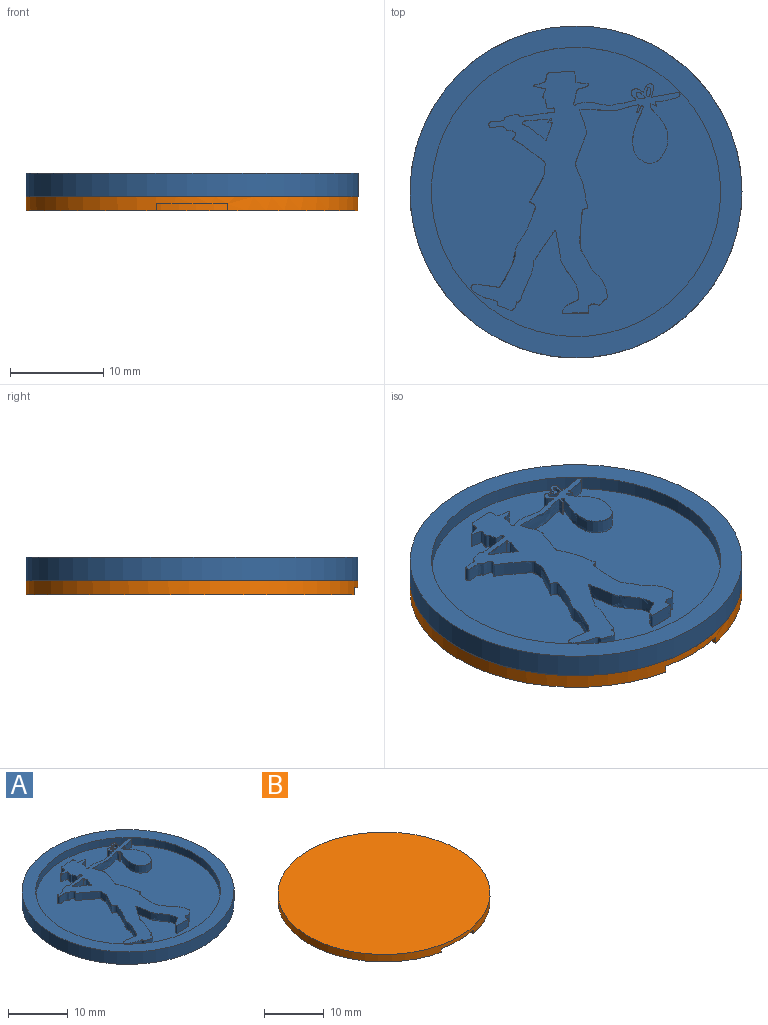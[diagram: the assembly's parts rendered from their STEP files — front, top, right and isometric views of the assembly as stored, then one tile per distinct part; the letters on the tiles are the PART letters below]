
ASSEMBLY  parts=2 mates=1
PART A: 13 faces, bbox 35.6x35.6x2.5 mm
  f0: plane 30.99x30.99mm, normal (0,0,1), area 683.6mm2, adj f4,f7
  f1: cylinder r=17.78mm len=35.56mm, axis (0,0,-1), area 283.8mm2, adj f2,f3
  f2: plane 35.56x35.56mm, normal (0,0,1), area 239mm2, adj f1,f4
  f3: plane 35.56x35.56mm, normal (0,0,-1), area 993.1mm2, adj f1
  f4: cylinder r=15.49mm len=30.99mm, axis (0,0,1), area 148.4mm2, adj f0,f2
  f5: plane 26x22.42mm, normal (0,0,1), area 87.5mm2, adj f6,f7,f8,f9
  f6: extruded ~1.52x1.02mm, area 3.8mm2, adj f5,f11
  f7: extruded ~25.78x19.35mm, area 227.5mm2, adj f0,f5
  f8: extruded ~1.52x1.02mm, area 4.2mm2, adj f5,f12
  f9: extruded ~3.18x2.29mm, area 14.9mm2, adj f5,f10
  f10: plane 3.23x2.33mm, normal (0,0,1), area 4mm2, adj f9
  f11: plane 1.03x0.46mm, normal (0,0,1), area 0.3mm2, adj f6
  f12: plane 1.03x0.75mm, normal (0,0,1), area 0.5mm2, adj f8
PART B: 170 faces, bbox 35.6x35.6x1.5 mm
  f0: plane 30.99x30.99mm, normal (0,0,-1), area 549.6mm2, adj f4,f5,f6,f7,f8,f9,f10,f11
  f1: plane 35.56x35.15mm, normal (0,0,-1), area 175mm2, adj f2,f165,f167,f169
  f2: cylinder r=17.78mm len=35.56mm, axis (0,0,-1), area 164.4mm2, adj f1,f3,f165,f167,f168
  f3: plane 35.56x35.56mm, normal (0,0,1), area 993.1mm2, adj f2
  f4: plane 1.49x0.76mm, normal (0,-1,0), area 1.1mm2, adj f0,f5,f15,f16
  f5: plane 7.05x0.76mm, normal (-1,0,0), area 5.4mm2, adj f0,f4,f6,f16
  f6: plane 1.49x0.76mm, normal (0,1,0), area 1.1mm2, adj f0,f5,f7,f16
  f7: plane 2.76x0.76mm, normal (1,0,0), area 2.1mm2, adj f0,f6,f8,f16
  f8: plane 2.79x0.76mm, normal (0,1,0), area 2.1mm2, adj f0,f7,f9,f16
  f9: plane 2.76x0.76mm, normal (-1,0,0), area 2.1mm2, adj f0,f8,f10,f16
  f10: plane 1.5x0.76mm, normal (0,1,0), area 1.1mm2, adj f0,f9,f11,f16
  f11: plane 7.05x0.76mm, normal (1,0,0), area 5.4mm2, adj f0,f10,f12,f16
  f12: plane 1.5x0.76mm, normal (0,-1,0), area 1.1mm2, adj f0,f11,f13,f16
  f13: plane 3.04x0.76mm, normal (-1,0,0), area 2.3mm2, adj f0,f12,f14,f16
  f14: plane 2.79x0.76mm, normal (0,-1,0), area 2.1mm2, adj f0,f13,f15,f16
  f15: plane 3.04x0.76mm, normal (1,0,0), area 2.3mm2, adj f0,f4,f14,f16
  f16: plane 7.05x5.78mm, normal (0,0,-1), area 24.5mm2, adj f4,f5,f6,f7,f8,f9,f10,f11
  f17: plane 7.05x0.76mm, normal (-1,0,0), area 5.4mm2, adj f0,f18,f41,f42
  f18: plane 2.19x0.76mm, normal (0,1,0), area 1.7mm2, adj f0,f17,f19,f42
  f19: extruded ~2.18x0.76mm, area 1.7mm2, adj f0,f18,f20,f42
  f20: extruded ~1.36x0.76mm, area 1.2mm2, adj f0,f19,f21,f42
  f21: extruded ~1.04x0.76mm, area 0.8mm2, adj f0,f20,f22,f42
  f22: extruded ~0.79x0.76mm, area 0.7mm2, adj f0,f21,f23,f42
  f23: plane 0.76x0.05mm, normal (1,0,0), area 0mm2, adj f0,f22,f24,f42
  f24: extruded ~0.97x0.76mm, area 0.9mm2, adj f0,f23,f25,f42
  f25: extruded ~1.09x0.76mm, area 0.9mm2, adj f0,f24,f26,f42
  f26: extruded ~1.51x0.76mm, area 1.3mm2, adj f0,f25,f27,f42
  f27: extruded ~1.89x0.76mm, area 1.5mm2, adj f0,f26,f41,f42
  f28: plane 0.93x0.76mm, normal (0,-1,0), area 0.7mm2, adj f29,f39,f42,f44
  f29: plane 1.84x0.76mm, normal (1,0,0), area 1.4mm2, adj f28,f30,f42,f44
  f30: plane 0.97x0.76mm, normal (0,1,0), area 0.7mm2, adj f29,f31,f42,f44
  f31: extruded ~0.91x0.76mm, area 0.7mm2, adj f30,f32,f42,f44
  f32: extruded ~0.76x0.72mm, area 0.6mm2, adj f31,f39,f42,f44
  f33: plane 1.57x0.76mm, normal (1,0,0), area 1.2mm2, adj f34,f40,f42,f43
  f34: plane 0.87x0.76mm, normal (0,1,0), area 0.7mm2, adj f33,f35,f42,f43
  f35: extruded ~0.88x0.76mm, area 0.7mm2, adj f34,f36,f42,f43
  f36: extruded ~0.76x0.62mm, area 0.5mm2, adj f35,f37,f42,f43
  f37: extruded ~0.76x0.58mm, area 0.5mm2, adj f36,f38,f42,f43
  f38: extruded ~0.94x0.76mm, area 0.7mm2, adj f37,f40,f42,f43
  f39: extruded ~1.25x0.88mm, area 1.3mm2, adj f28,f32,f42,f44
  f40: plane 0.79x0.76mm, normal (0,-1,0), area 0.6mm2, adj f33,f38,f42,f43
  f41: plane 2.64x0.76mm, normal (0,-1,0), area 2mm2, adj f0,f17,f27,f42
  f42: plane 7.05x5.23mm, normal (0,0,-1), area 27.1mm2, adj f17,f18,f19,f20,f21,f22,f23,f24
  f43: plane 2.02x1.57mm, normal (0,0,-1), area 2.9mm2, adj f33,f34,f35,f36,f37,f38,f40
  f44: plane 2.18x1.84mm, normal (0,0,-1), area 3.6mm2, adj f28,f29,f30,f31,f32,f39
  f45: extruded ~2.44x2.09mm, area 2.8mm2, adj f0,f46,f52,f53
  f46: extruded ~2.44x2.09mm, area 2.8mm2, adj f0,f45,f47,f53
  f47: extruded ~2.41x2.09mm, area 2.7mm2, adj f0,f46,f52,f53
  f48: extruded ~1.63x1.14mm, area 1.7mm2, adj f49,f51,f53,f54
  f49: extruded ~1.63x1.14mm, area 1.7mm2, adj f48,f50,f53,f54
  f50: extruded ~1.6x1.14mm, area 1.7mm2, adj f49,f51,f53,f54
  f51: extruded ~1.6x1.14mm, area 1.7mm2, adj f48,f50,f53,f54
  f52: extruded ~2.41x2.09mm, area 2.7mm2, adj f0,f45,f47,f53
  f53: plane 4.85x4.18mm, normal (0,0,-1), area 10.4mm2, adj f45,f46,f47,f48,f49,f50,f51,f52
  f54: plane 3.24x2.27mm, normal (0,0,-1), area 6mm2, adj f48,f49,f50,f51
  f55: extruded ~1.45x0.82mm, area 1.3mm2, adj f0,f56,f62,f63
  f56: extruded ~1.6x1.45mm, area 1.9mm2, adj f0,f55,f57,f63
  f57: plane 3.16x0.76mm, normal (-1,0,0), area 2.4mm2, adj f0,f56,f58,f63
  f58: plane 0.93x0.76mm, normal (0,1,0), area 0.7mm2, adj f0,f57,f59,f63
  f59: plane 3.09x0.76mm, normal (1,0,0), area 2.4mm2, adj f0,f58,f60,f63
  f60: extruded ~0.86x0.76mm, area 0.9mm2, adj f0,f59,f61,f63
  f61: extruded ~0.76x0.69mm, area 0.7mm2, adj f0,f60,f62,f63
  f62: plane 0.76x0.64mm, normal (0.59,0.81,0), area 0.6mm2, adj f0,f55,f61,f63
  f63: plane 4.76x2.9mm, normal (0,0,-1), area 5.6mm2, adj f55,f56,f57,f58,f59,f60,f61,f62
  f64: extruded ~2.19x1.82mm, area 2.5mm2, adj f0,f65,f73,f74
  f65: extruded ~2.19x1.81mm, area 2.5mm2, adj f0,f64,f66,f74
  f66: plane 2.57x0.76mm, normal (-1,0,0), area 2mm2, adj f0,f65,f67,f74
  f67: plane 0.9x0.76mm, normal (0,1,0), area 0.7mm2, adj f0,f66,f68,f74
  f68: plane 2.65x0.76mm, normal (1,0,0), area 2mm2, adj f0,f67,f69,f74
  f69: extruded ~1.3x0.91mm, area 1.4mm2, adj f0,f68,f70,f74
  f70: extruded ~1.3x0.88mm, area 1.4mm2, adj f0,f69,f71,f74
  f71: plane 2.65x0.76mm, normal (-1,0,0), area 2mm2, adj f0,f70,f72,f74
  f72: plane 0.93x0.76mm, normal (0,1,0), area 0.7mm2, adj f0,f71,f73,f74
  f73: plane 2.57x0.76mm, normal (1,0,0), area 2mm2, adj f0,f64,f72,f74
  f74: plane 4.76x3.62mm, normal (0,0,-1), area 9.2mm2, adj f64,f65,f66,f67,f68,f69,f70,f71
  f75: plane 4.67x0.76mm, normal (1,0,0), area 3.6mm2, adj f0,f76,f90,f91
  f76: plane 0.88x0.76mm, normal (0,-1,0), area 0.7mm2, adj f0,f75,f77,f91
  f77: plane 1.88x0.76mm, normal (-1,0,0), area 1.4mm2, adj f0,f76,f78,f91
  f78: extruded ~1.63x0.76mm, area 1.2mm2, adj f0,f77,f79,f91
  f79: plane 0.76x0.03mm, normal (0,-1,0), area 0mm2, adj f0,f78,f80,f91
  f80: plane 1x0.76mm, normal (0.9,-0.43,0), area 0.8mm2, adj f0,f79,f81,f91
  f81: plane 2.5x1.35mm, normal (0.88,-0.48,0), area 2.2mm2, adj f0,f80,f82,f91
  f82: plane 0.95x0.76mm, normal (0,-1,0), area 0.7mm2, adj f0,f81,f83,f91
  f83: plane 4.67x0.76mm, normal (-1,0,0), area 3.6mm2, adj f0,f82,f84,f91
  f84: plane 0.88x0.76mm, normal (0,1,0), area 0.7mm2, adj f0,f83,f85,f91
  f85: plane 1.86x0.76mm, normal (1,0,0), area 1.4mm2, adj f0,f84,f86,f91
  f86: extruded ~1.64x0.76mm, area 1.3mm2, adj f0,f85,f87,f91
  f87: plane 0.76x0.03mm, normal (0,1,0), area 0mm2, adj f0,f86,f88,f91
  f88: plane 1.01x0.76mm, normal (-0.91,0.42,0), area 0.8mm2, adj f0,f87,f89,f91
  f89: plane 2.49x1.36mm, normal (-0.88,0.48,0), area 2.2mm2, adj f0,f88,f90,f91
  f90: plane 0.95x0.76mm, normal (0,1,0), area 0.7mm2, adj f0,f75,f89,f91
  f91: plane 4.67x3.57mm, normal (0,0,-1), area 10.9mm2, adj f75,f76,f77,f78,f79,f80,f81,f82
  f92: plane 2.41x1.31mm, normal (0.88,0.48,0), area 2.1mm2, adj f0,f93,f109,f110
  f93: plane 0.99x0.76mm, normal (0,-1,0), area 0.8mm2, adj f0,f92,f94,f110
  f94: plane 1.04x0.76mm, normal (-0.9,-0.43,0), area 0.9mm2, adj f0,f93,f95,f110
  f95: extruded ~0.77x0.76mm, area 0.6mm2, adj f0,f94,f96,f110
  f96: plane 0.76x0.02mm, normal (0,-1,0), area 0mm2, adj f0,f95,f97,f110
  f97: extruded ~0.77x0.76mm, area 0.6mm2, adj f0,f96,f98,f110
  f98: plane 1.04x0.76mm, normal (0.89,-0.45,0), area 0.9mm2, adj f0,f97,f99,f110
  f99: plane 1.04x0.76mm, normal (0,-1,0), area 0.8mm2, adj f0,f98,f100,f110
  f100: plane 2.37x1.31mm, normal (-0.87,0.48,0), area 2.1mm2, adj f0,f99,f101,f110
  f101: plane 2.3x1.23mm, normal (-0.88,-0.47,0), area 2mm2, adj f0,f100,f102,f110
  f102: plane 0.98x0.76mm, normal (0,1,0), area 0.8mm2, adj f0,f101,f103,f110
  f103: plane 0.96x0.76mm, normal (0.91,0.42,0), area 0.8mm2, adj f0,f102,f104,f110
  f104: extruded ~0.76x0.74mm, area 0.6mm2, adj f0,f103,f105,f110
  f105: plane 0.76x0.03mm, normal (0,1,0), area 0mm2, adj f0,f104,f106,f110
  f106: extruded ~0.76x0.74mm, area 0.6mm2, adj f0,f105,f107,f110
  f107: plane 0.96x0.76mm, normal (-0.9,0.44,0), area 0.8mm2, adj f0,f106,f108,f110
  f108: plane 1.04x0.76mm, normal (0,1,0), area 0.8mm2, adj f0,f107,f109,f110
  f109: plane 2.26x1.23mm, normal (0.88,-0.48,0), area 2mm2, adj f0,f92,f108,f110
  f110: plane 4.67x3.78mm, normal (0,0,-1), area 8.4mm2, adj f92,f93,f94,f95,f96,f97,f98,f99
  f111: plane 4.67x0.76mm, normal (1,0,0), area 3.6mm2, adj f0,f112,f114,f115
  f112: plane 0.94x0.76mm, normal (0,-1,0), area 0.7mm2, adj f0,f111,f113,f115
  f113: plane 4.67x0.76mm, normal (-1,0,0), area 3.6mm2, adj f0,f112,f114,f115
  f114: plane 0.94x0.76mm, normal (0,1,0), area 0.7mm2, adj f0,f111,f113,f115
  f115: plane 4.67x0.94mm, normal (0,0,-1), area 4.4mm2, adj f111,f112,f113,f114
  f116: plane 4.67x0.76mm, normal (1,0,0), area 3.6mm2, adj f0,f117,f131,f132
  f117: plane 0.88x0.76mm, normal (0,-1,0), area 0.7mm2, adj f0,f116,f118,f132
  f118: plane 1.88x0.76mm, normal (-1,0,0), area 1.4mm2, adj f0,f117,f119,f132
  f119: extruded ~1.63x0.76mm, area 1.2mm2, adj f0,f118,f120,f132
  f120: plane 0.76x0.03mm, normal (0,-1,0), area 0mm2, adj f0,f119,f121,f132
  f121: plane 1x0.76mm, normal (0.9,-0.43,0), area 0.8mm2, adj f0,f120,f122,f132
  f122: plane 2.5x1.35mm, normal (0.88,-0.48,0), area 2.2mm2, adj f0,f121,f123,f132
  f123: plane 0.95x0.76mm, normal (0,-1,0), area 0.7mm2, adj f0,f122,f124,f132
  f124: plane 4.67x0.76mm, normal (-1,0,0), area 3.6mm2, adj f0,f123,f125,f132
  f125: plane 0.88x0.76mm, normal (0,1,0), area 0.7mm2, adj f0,f124,f126,f132
  f126: plane 1.86x0.76mm, normal (1,0,0), area 1.4mm2, adj f0,f125,f127,f132
  f127: extruded ~1.64x0.76mm, area 1.3mm2, adj f0,f126,f128,f132
  f128: plane 0.76x0.03mm, normal (0,1,0), area 0mm2, adj f0,f127,f129,f132
  f129: plane 1.01x0.76mm, normal (-0.91,0.42,0), area 0.8mm2, adj f0,f128,f130,f132
  f130: plane 2.49x1.36mm, normal (-0.88,0.48,0), area 2.2mm2, adj f0,f129,f131,f132
  f131: plane 0.95x0.76mm, normal (0,1,0), area 0.7mm2, adj f0,f116,f130,f132
  f132: plane 4.67x3.57mm, normal (0,0,-1), area 10.9mm2, adj f116,f117,f118,f119,f120,f121,f122,f123
  f133: extruded ~1.78x0.76mm, area 1.4mm2, adj f134,f146,f147,f163
  f134: extruded ~1.78x0.76mm, area 1.4mm2, adj f133,f135,f147,f163
  f135: extruded ~1.35x0.76mm, area 1.2mm2, adj f134,f136,f147,f163
  f136: extruded ~2.38x1.78mm, area 2.6mm2, adj f135,f137,f147,f163
  f137: extruded ~2.38x1.79mm, area 2.6mm2, adj f136,f146,f147,f163
  f138: extruded ~2.69x0.87mm, area 2.2mm2, adj f0,f139,f145,f147
  f139: extruded ~2.69x0.86mm, area 2.2mm2, adj f0,f138,f140,f147
  f140: extruded ~2.49x0.94mm, area 2.1mm2, adj f0,f139,f141,f147
  f141: extruded ~2.5x0.93mm, area 2.1mm2, adj f0,f140,f142,f147
  f142: extruded ~2.69x0.87mm, area 2.2mm2, adj f0,f141,f143,f147
  f143: extruded ~2.7x0.87mm, area 2.2mm2, adj f0,f142,f144,f147
  f144: extruded ~2.49x0.94mm, area 2.1mm2, adj f0,f143,f145,f147
  f145: extruded ~2.49x0.94mm, area 2.1mm2, adj f0,f138,f144,f147
  f146: extruded ~1.34x0.76mm, area 1.2mm2, adj f133,f137,f147,f163
  f147: plane 7.26x6.71mm, normal (0,0,-1), area 26mm2, adj f133,f134,f135,f136,f137,f138,f139,f140
  f148: extruded ~1.78x0.76mm, area 1.4mm2, adj f149,f161,f162,f164
  f149: extruded ~1.78x0.76mm, area 1.4mm2, adj f148,f150,f162,f164
  f150: extruded ~1.35x0.76mm, area 1.2mm2, adj f149,f151,f162,f164
  f151: extruded ~2.38x1.78mm, area 2.6mm2, adj f150,f152,f162,f164
  f152: extruded ~2.38x1.79mm, area 2.6mm2, adj f151,f161,f162,f164
  f153: extruded ~2.69x0.87mm, area 2.2mm2, adj f0,f154,f160,f162
  f154: extruded ~2.69x0.86mm, area 2.2mm2, adj f0,f153,f155,f162
  f155: extruded ~2.49x0.94mm, area 2.1mm2, adj f0,f154,f156,f162
  f156: extruded ~2.5x0.93mm, area 2.1mm2, adj f0,f155,f157,f162
  f157: extruded ~2.69x0.87mm, area 2.2mm2, adj f0,f156,f158,f162
  f158: extruded ~2.7x0.87mm, area 2.2mm2, adj f0,f157,f159,f162
  f159: extruded ~2.49x0.94mm, area 2.1mm2, adj f0,f158,f160,f162
  f160: extruded ~2.49x0.94mm, area 2.1mm2, adj f0,f153,f159,f162
  f161: extruded ~1.34x0.76mm, area 1.2mm2, adj f148,f152,f162,f164
  f162: plane 7.26x6.71mm, normal (0,0,-1), area 26mm2, adj f148,f149,f150,f151,f152,f153,f154,f155
  f163: plane 4.76x3.58mm, normal (0,0,-1), area 14.2mm2, adj f133,f134,f135,f136,f137,f146
  f164: plane 4.76x3.58mm, normal (0,0,-1), area 14.2mm2, adj f148,f149,f150,f151,f152,f161
  f165: plane 1.83x0.76mm, normal (1,0,0), area 1.4mm2, adj f1,f2,f168,f169
  f166: cylinder r=15.49mm len=30.99mm, axis (0,0,-1), area 74.2mm2, adj f0,f168
  f167: plane 1.83x0.76mm, normal (-1,0,0), area 1.4mm2, adj f1,f2,f168,f169
  f168: plane 33.78x32mm, normal (0,0,-1), area 63.9mm2, adj f2,f165,f166,f167,f169
  f169: cylinder r=16mm len=32mm, axis (0,0,-1), area 70.8mm2, adj f1,f165,f167,f168
PLACE A t=(-6.45,-25.08,-32.14)mm fixed
PLACE B t=(-6.45,-25.08,-33.67)mm
MATE fastened B.f2 <-> A.f1  axis (0,0,1) through (-6.45,-25.08,-32.14)mm
